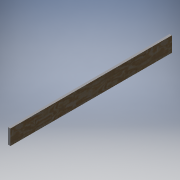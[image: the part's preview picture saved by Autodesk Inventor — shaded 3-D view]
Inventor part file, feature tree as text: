
AUTODESK INVENTOR PART (.ipt)
format: ipt  version: 2018.2 (Build 222227000, 227)  size: 141,312 bytes
history: native  units: in
note: dims shown in document units (in); Inventor stores cm internally (conversion verified against a paired STEP export)
features: extrude x1, sketch x1
ambient origin geometry x8: Origin, YZ Plane, XZ Plane, XY Plane, X Axis, Y Axis, Z Axis, Center Point
bodies: Solid1 (feature_tree)
feature tree (2):
  extrude  "Extrusion1"  [1 undecoded]
  sketch  "Sketch1"  dims[d0=0.75in d1=0.0in]
note: 1 required parameter value undecoded (feature->parameter linkage not recoverable at this tier; creation-order binding heuristic only, values carry confidence <= 0.55)
